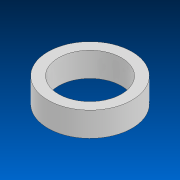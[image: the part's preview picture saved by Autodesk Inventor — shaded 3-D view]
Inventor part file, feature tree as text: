
AUTODESK INVENTOR PART (.ipt)
format: ipt  version: 2022 (Build 260153000, 153)  size: 84,480 bytes
history: native  units: in
note: dims shown in document units (in); Inventor stores cm internally (conversion verified against a paired STEP export)
features: extrude x1, sketch x1
ambient origin geometry x8: Origin, YZ Plane, XZ Plane, XY Plane, X Axis, Y Axis, Z Axis, Center Point
bodies: Solid1 (feature_tree)
feature tree (2):
  extrude  "Extrusion1"  Depth=0.436in
  sketch  "Sketch1"  dims[d0=1.125in d1=1.5in d2=0.436in d3=0.0in]
